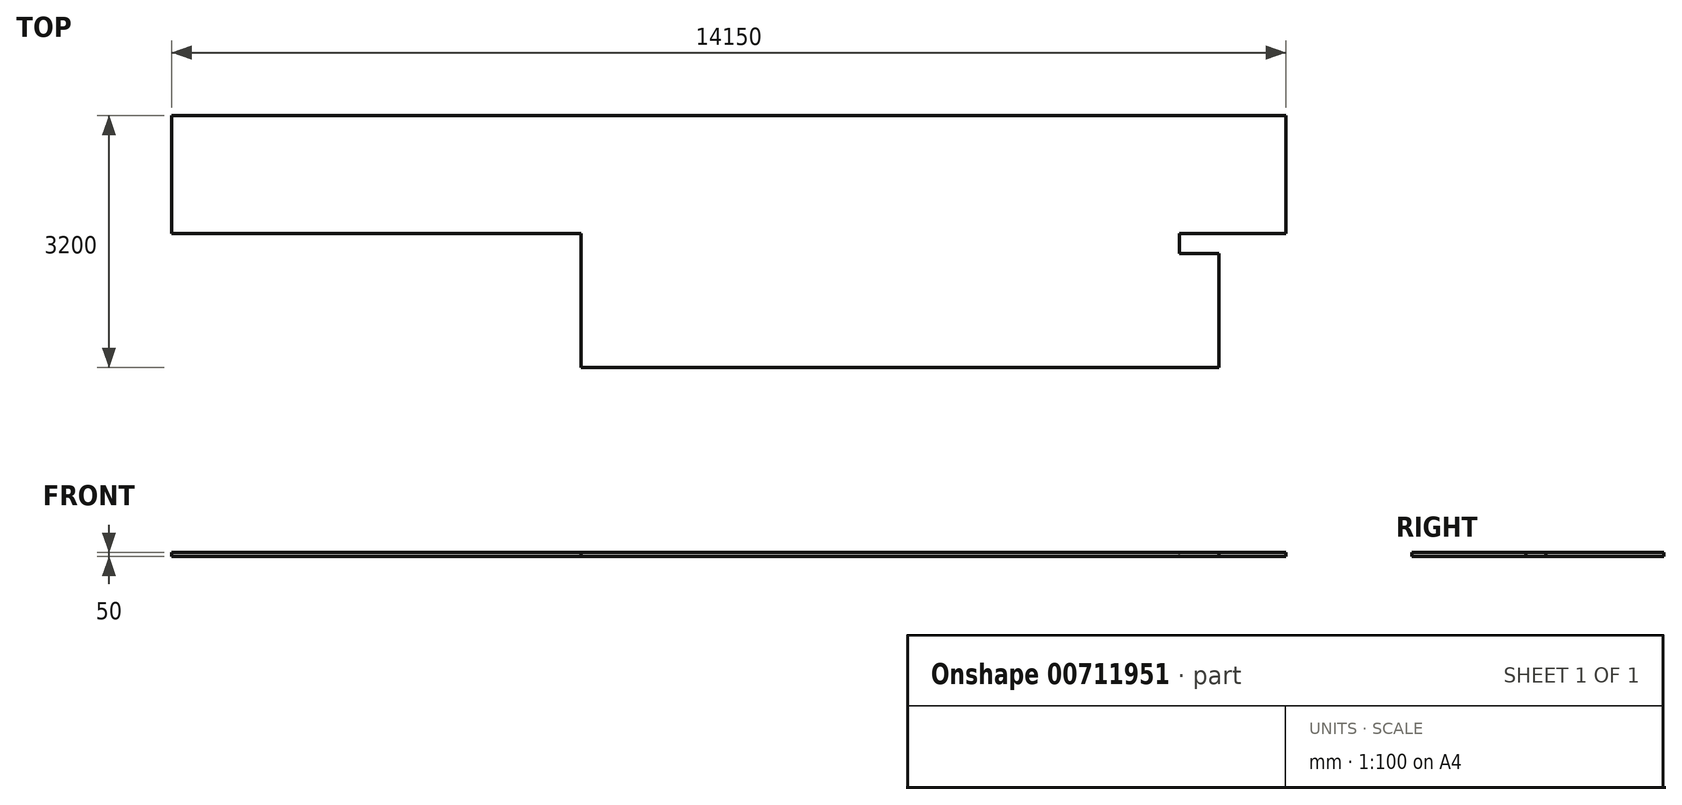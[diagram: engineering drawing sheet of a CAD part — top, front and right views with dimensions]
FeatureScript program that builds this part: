
annotation { "Feature Type Name" : "Feature", "Feature Type Description" : "" }
export const myFeature = defineFeature(function(context is Context, id is Id, definition is map)
    precondition{}
    {
        {
            var Q0;
            Q0=qCreatedBy(makeId("Top.planeOp"),FACE);
            var sketch = newSketch(context, id + "F0", { "sketchPlane" : qUnion([Q0])});
            skLineSegment(sketch, "E0", {"start": v(-4402.74, 0) * mm, "end": v(-4402.74, 1500) * mm});
            skLineSegment(sketch, "E1", {"start": v(-4402.74, 1500) * mm, "end": v(9747.26, 1500) * mm});
            skLineSegment(sketch, "E2", {"start": v(9747.26, 1500) * mm, "end": v(9747.26, 0) * mm});
            skLineSegment(sketch, "E3", {"start": v(9747.26, 0) * mm, "end": v(8397.26, 0) * mm});
            skLineSegment(sketch, "E4", {"start": v(8397.26, 0) * mm, "end": v(8397.26, 0) * mm});
            skLineSegment(sketch, "E5", {"start": v(8897.26, -1700) * mm, "end": v(797.26, -1700) * mm});
            skLineSegment(sketch, "E6", {"start": v(797.26, -1700) * mm, "end": v(797.26, 0) * mm});
            skLineSegment(sketch, "E7", {"start": v(797.26, 0) * mm, "end": v(-4402.74, 0) * mm});
            skLineSegment(sketch, "E8", {"start": v(8397.26, 0) * mm, "end": v(8397.26, -250) * mm});
            skLineSegment(sketch, "E9", {"start": v(8397.26, -250) * mm, "end": v(8897.26, -250) * mm});
            skLineSegment(sketch, "E10", {"start": v(8897.26, -250) * mm, "end": v(8897.26, -1700) * mm});
            skSolve(sketch);
        }
        {
            var Q0;
            Q0 = qSketchRegion(id + "F0", true);
            extrude(context, id + "F1", {"entities" : qUnion([Q0]), "depth" : -50 * mm, "offsetDistance" : 25 * mm});
        }
    });
